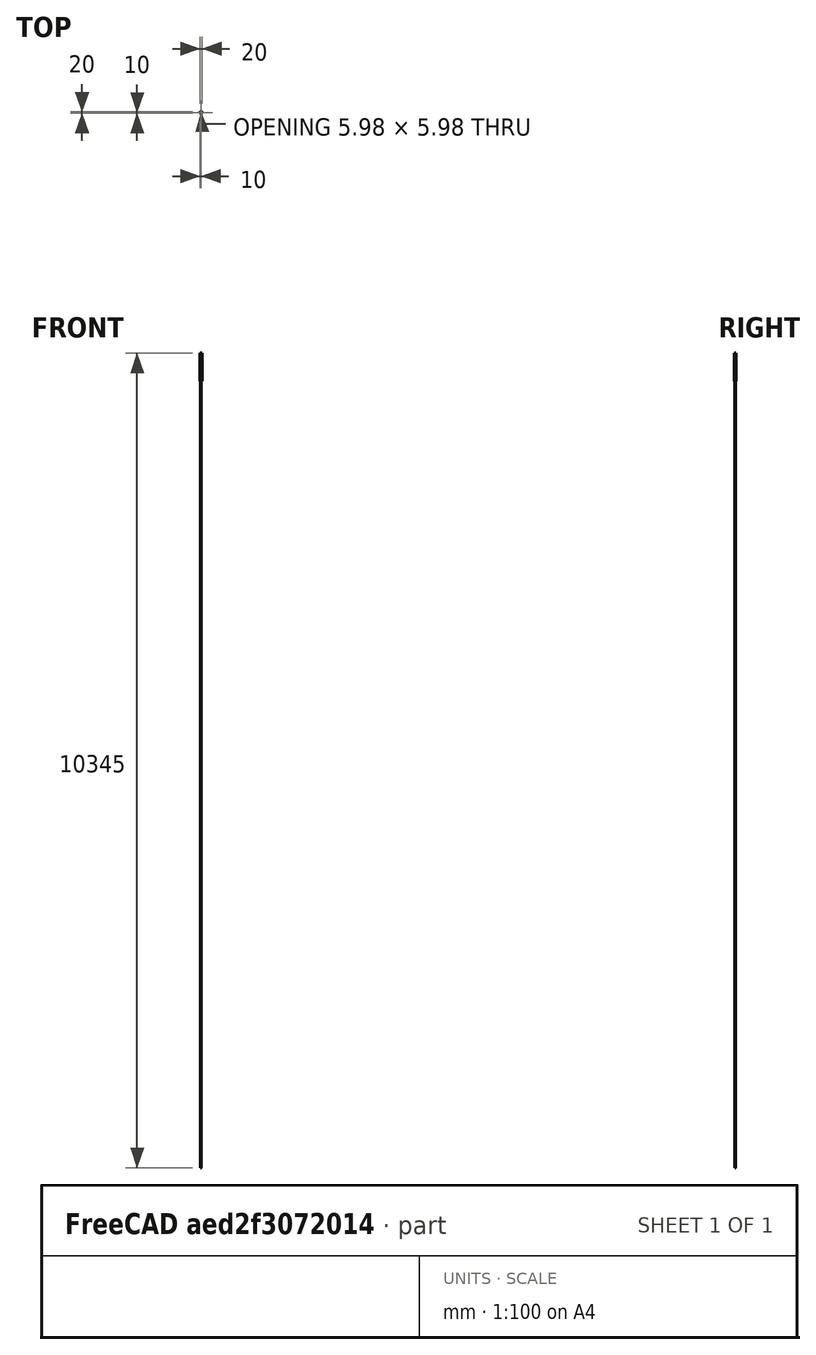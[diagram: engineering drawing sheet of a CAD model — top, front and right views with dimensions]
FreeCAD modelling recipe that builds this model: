
FCSTD DOCUMENT  (FreeCAD 0.15R4671 (Git))
Label: Perfil 350mm
License: CC-BY 3.0
LicenseURL: http://creativecommons.org/licenses/by/3.0/
objects: Sketcher::SketchObject×2, Part::Extrusion×2, PartDesign::Pad×1, PartDesign::Pocket×1, Part::Cut×1
note: 9 computed .brp shape members not serialized (recipe doc carries the construction recipe); baked Part::Feature solids carry a one-line shape summary decoded from their .brp

FEATURE [Sketcher::SketchObject] Sketch
  Placement = pos=(1.5,0,0) rot=(0,0,1;0rad)
  sketch-geometry (136):
    g0: LineSegment StartX=0 StartY=20 StartZ=0 EndX=4.65 EndY=20 EndZ=0
    g1: ArcOfCircle CenterX=-1e-12 CenterY=18.5 CenterZ=0 NormalX=0 NormalY=0 NormalZ=1 Radius=1.5 StartAngle=1.5708 EndAngle=3.14159
    g2: LineSegment StartX=-1.5 StartY=13.85 StartZ=0 EndX=-1.5 EndY=18.5 EndZ=0
    g3: ArcOfCircle CenterX=-1.3 CenterY=13.85 CenterZ=0 NormalX=0 NormalY=0 NormalZ=1 Radius=0.2 StartAngle=3.14159 EndAngle=4.71239
    g4: LineSegment StartX=-1 StartY=13.65 StartZ=0 EndX=-1.3 EndY=13.65 EndZ=0
    g5: LineSegment StartX=-1 StartY=13.3 StartZ=0 EndX=-1 EndY=13.65 EndZ=0
    g6: ArcOfCircle CenterX=-0.8 CenterY=13.3 CenterZ=0 NormalX=0 NormalY=0 NormalZ=1 Radius=0.2 StartAngle=3.14159 EndAngle=4.71239
    g7: LineSegment StartX=-0.5 StartY=13.1 StartZ=0 EndX=-0.8 EndY=13.1 EndZ=0
    g8: ArcOfCircle CenterX=-0.5 CenterY=13.6 CenterZ=0 NormalX=0 NormalY=0 NormalZ=1 Radius=0.5 StartAngle=4.71239 EndAngle=6.28319
    g9: LineSegment StartX=2.68e-07 StartY=15.5 StartZ=0 EndX=2.68e-07 EndY=13.6 EndZ=0
    g10: ArcOfCircle CenterX=0.5 CenterY=15.5 CenterZ=0 NormalX=0 NormalY=0 NormalZ=1 Radius=0.5 StartAngle=1.5708 EndAngle=3.14159
    g11: LineSegment StartX=1.23223 StartY=16 StartZ=0 EndX=0.5 EndY=16 EndZ=0
    g12: ArcOfCircle CenterX=1.23223 CenterY=15.5 CenterZ=0 NormalX=0 NormalY=0 NormalZ=1 Radius=0.5 StartAngle=0.785398 EndAngle=1.5708
    g13: LineSegment StartX=3.85355 StartY=13.5858 StartZ=0 EndX=1.58579 EndY=15.8536 EndZ=0
    g14: ArcOfCircle CenterX=3.5 CenterY=13.2322 CenterZ=0 NormalX=0 NormalY=0 NormalZ=1 Radius=0.5 StartAngle=0 EndAngle=0.785398
    g15: LineSegment StartX=4 StartY=10.9536 StartZ=0 EndX=4 EndY=13.2322 EndZ=0
    g16: ArcOfCircle CenterX=4.2 CenterY=10.9536 CenterZ=0 NormalX=0 NormalY=0 NormalZ=1 Radius=0.2 StartAngle=3.14159 EndAngle=3.66519
    g17: LineSegment StartX=4.46188 StartY=10.1 StartZ=0 EndX=4.0268 EndY=10.8536 EndZ=0
    g18: ArcOfCircle CenterX=4.28868 CenterY=10 CenterZ=0 NormalX=0 NormalY=0 NormalZ=1 Radius=0.2 StartAngle=5.75959 EndAngle=6.80678
    g19: LineSegment StartX=4.0268 StartY=9.14641 StartZ=0 EndX=4.46188 EndY=9.9 EndZ=0
    g20: ArcOfCircle CenterX=4.2 CenterY=9.04641 CenterZ=0 NormalX=0 NormalY=0 NormalZ=1 Radius=0.2 StartAngle=2.61799 EndAngle=3.14159
    g21: LineSegment StartX=4 StartY=6.76777 StartZ=0 EndX=4 EndY=9.04641 EndZ=0
    g22: ArcOfCircle CenterX=3.5 CenterY=6.76777 CenterZ=0 NormalX=0 NormalY=0 NormalZ=1 Radius=0.5 StartAngle=5.49779 EndAngle=6.28319
    g23: LineSegment StartX=1.58579 StartY=4.14645 StartZ=0 EndX=3.85355 EndY=6.41421 EndZ=0
    g24: ArcOfCircle CenterX=1.23223 CenterY=4.5 CenterZ=0 NormalX=0 NormalY=0 NormalZ=1 Radius=0.5 StartAngle=4.71239 EndAngle=5.49779
    g25: LineSegment StartX=0.5 StartY=4 StartZ=0 EndX=1.23223 EndY=4 EndZ=0
    g26: ArcOfCircle CenterX=0.5 CenterY=4.5 CenterZ=0 NormalX=0 NormalY=0 NormalZ=1 Radius=0.5 StartAngle=3.14159 EndAngle=4.71239
    g27: LineSegment StartX=2.68e-07 StartY=6.4 StartZ=0 EndX=2.68e-07 EndY=4.5 EndZ=0
    g28: ArcOfCircle CenterX=-0.5 CenterY=6.4 CenterZ=0 NormalX=0 NormalY=0 NormalZ=1 Radius=0.5 StartAngle=0 EndAngle=1.5708
    g29: LineSegment StartX=-0.8 StartY=6.9 StartZ=0 EndX=-0.5 EndY=6.9 EndZ=0
    g30: ArcOfCircle CenterX=-0.8 CenterY=6.7 CenterZ=0 NormalX=0 NormalY=0 NormalZ=1 Radius=0.2 StartAngle=1.5708 EndAngle=3.14159
    g31: LineSegment StartX=-1 StartY=6.35 StartZ=0 EndX=-1 EndY=6.7 EndZ=0
    g32: LineSegment StartX=-1.3 StartY=6.35 StartZ=0 EndX=-1 EndY=6.35 EndZ=0
    g33: ArcOfCircle CenterX=-1.3 CenterY=6.15 CenterZ=0 NormalX=0 NormalY=0 NormalZ=1 Radius=0.2 StartAngle=1.5708 EndAngle=3.14159
    g34: LineSegment StartX=-1.5 StartY=1.5 StartZ=0 EndX=-1.5 EndY=6.15 EndZ=0
    g35: ArcOfCircle CenterX=0 CenterY=1.5 CenterZ=0 NormalX=0 NormalY=0 NormalZ=1 Radius=1.5 StartAngle=3.14159 EndAngle=4.71239
    g36: LineSegment StartX=4.65 StartY=1e-12 StartZ=0 EndX=0 EndY=0 EndZ=0
    g37: ArcOfCircle CenterX=4.65 CenterY=0.2 CenterZ=0 NormalX=0 NormalY=0 NormalZ=1 Radius=0.2 StartAngle=4.71239 EndAngle=6.28319
    g38: LineSegment StartX=4.85 StartY=0.5 StartZ=0 EndX=4.85 EndY=0.2 EndZ=0
    g39: LineSegment StartX=5.2 StartY=0.5 StartZ=0 EndX=4.85 EndY=0.5 EndZ=0
    g40: ArcOfCircle CenterX=5.2 CenterY=0.7 CenterZ=0 NormalX=0 NormalY=0 NormalZ=1 Radius=0.2 StartAngle=4.71239 EndAngle=6.28319
    g41: LineSegment StartX=5.4 StartY=1 StartZ=0 EndX=5.4 EndY=0.7 EndZ=0
    g42: ArcOfCircle CenterX=4.9 CenterY=1 CenterZ=0 NormalX=0 NormalY=0 NormalZ=1 Radius=0.5 StartAngle=0 EndAngle=1.5708
    g43: LineSegment StartX=3 StartY=1.5 StartZ=0 EndX=4.9 EndY=1.5 EndZ=0
    g44: ArcOfCircle CenterX=3 CenterY=2 CenterZ=0 NormalX=0 NormalY=0 NormalZ=1 Radius=0.5 StartAngle=3.14159 EndAngle=4.71239
    g45: LineSegment StartX=2.5 StartY=2.73223 StartZ=0 EndX=2.5 EndY=2 EndZ=0
    g46: ArcOfCircle CenterX=3 CenterY=2.73223 CenterZ=0 NormalX=0 NormalY=0 NormalZ=1 Radius=0.5 StartAngle=2.35619 EndAngle=3.14159
    g47: LineSegment StartX=4.91421 StartY=5.35355 StartZ=0 EndX=2.64645 EndY=3.08579 EndZ=0
    g48: ArcOfCircle CenterX=5.26777 CenterY=5 CenterZ=0 NormalX=0 NormalY=0 NormalZ=1 Radius=0.5 StartAngle=1.5708 EndAngle=2.35619
    g49: LineSegment StartX=7.54641 StartY=5.5 StartZ=0 EndX=5.26777 EndY=5.5 EndZ=0
    g50: ArcOfCircle CenterX=7.54641 CenterY=5.7 CenterZ=0 NormalX=0 NormalY=0 NormalZ=1 Radius=0.2 StartAngle=4.71239 EndAngle=5.23599
    g51: LineSegment StartX=8.4 StartY=5.96188 StartZ=0 EndX=7.64641 EndY=5.52679 EndZ=0
    g52: ArcOfCircle CenterX=8.5 CenterY=5.78868 CenterZ=0 NormalX=0 NormalY=0 NormalZ=1 Radius=0.2 StartAngle=1.0472 EndAngle=2.0944
    g53: LineSegment StartX=9.35359 StartY=5.52679 StartZ=0 EndX=8.6 EndY=5.96188 EndZ=0
    g54: ArcOfCircle CenterX=9.45359 CenterY=5.7 CenterZ=0 NormalX=0 NormalY=0 NormalZ=1 Radius=0.2 StartAngle=4.18879 EndAngle=4.71239
    g55: LineSegment StartX=11.7322 StartY=5.5 StartZ=0 EndX=9.45359 EndY=5.5 EndZ=0
    g56: ArcOfCircle CenterX=11.7322 CenterY=5 CenterZ=0 NormalX=0 NormalY=0 NormalZ=1 Radius=0.5 StartAngle=0.785398 EndAngle=1.5708
    g57: LineSegment StartX=14.3536 StartY=3.08579 StartZ=0 EndX=12.0858 EndY=5.35355 EndZ=0
    g58: ArcOfCircle CenterX=14 CenterY=2.73223 CenterZ=0 NormalX=0 NormalY=0 NormalZ=1 Radius=0.5 StartAngle=0 EndAngle=0.785398
    g59: LineSegment StartX=14.5 StartY=2 StartZ=0 EndX=14.5 EndY=2.73223 EndZ=0
    g60: ArcOfCircle CenterX=14 CenterY=2 CenterZ=0 NormalX=0 NormalY=0 NormalZ=1 Radius=0.5 StartAngle=4.71239 EndAngle=6.28319
    g61: LineSegment StartX=12.1 StartY=1.5 StartZ=0 EndX=14 EndY=1.5 EndZ=0
    g62: ArcOfCircle CenterX=12.1 CenterY=1 CenterZ=0 NormalX=0 NormalY=0 NormalZ=1 Radius=0.5 StartAngle=1.5708 EndAngle=3.14159
    g63: LineSegment StartX=11.6 StartY=0.7 StartZ=0 EndX=11.6 EndY=1 EndZ=0
    g64: ArcOfCircle CenterX=11.8 CenterY=0.7 CenterZ=0 NormalX=0 NormalY=0 NormalZ=1 Radius=0.2 StartAngle=3.14159 EndAngle=4.71239
    g65: LineSegment StartX=12.15 StartY=0.5 StartZ=0 EndX=11.8 EndY=0.5 EndZ=0
    g66: LineSegment StartX=12.15 StartY=0.2 StartZ=0 EndX=12.15 EndY=0.5 EndZ=0
    g67: ArcOfCircle CenterX=12.35 CenterY=0.2 CenterZ=0 NormalX=0 NormalY=0 NormalZ=1 Radius=0.2 StartAngle=3.14159 EndAngle=4.71239
    g68: LineSegment StartX=17 StartY=1e-12 StartZ=0 EndX=12.35 EndY=0 EndZ=0
    g69: ArcOfCircle CenterX=17 CenterY=1.5 CenterZ=0 NormalX=0 NormalY=0 NormalZ=1 Radius=1.5 StartAngle=4.71239 EndAngle=6.28319
    g70: LineSegment StartX=18.5 StartY=6.15 StartZ=0 EndX=18.5 EndY=1.5 EndZ=0
    g71: ArcOfCircle CenterX=18.3 CenterY=6.15 CenterZ=0 NormalX=0 NormalY=0 NormalZ=1 Radius=0.2 StartAngle=0 EndAngle=1.5708
    g72: LineSegment StartX=18 StartY=6.35 StartZ=0 EndX=18.3 EndY=6.35 EndZ=0
    g73: LineSegment StartX=18 StartY=6.7 StartZ=0 EndX=18 EndY=6.35 EndZ=0
    g74: ArcOfCircle CenterX=17.8 CenterY=6.7 CenterZ=0 NormalX=0 NormalY=0 NormalZ=1 Radius=0.2 StartAngle=0 EndAngle=1.5708
    g75: LineSegment StartX=17.5 StartY=6.9 StartZ=0 EndX=17.8 EndY=6.9 EndZ=0
    g76: ArcOfCircle CenterX=17.5 CenterY=6.4 CenterZ=0 NormalX=0 NormalY=0 NormalZ=1 Radius=0.5 StartAngle=1.5708 EndAngle=3.14159
    g77: LineSegment StartX=17 StartY=4.5 StartZ=0 EndX=17 EndY=6.4 EndZ=0
    g78: ArcOfCircle CenterX=16.5 CenterY=4.5 CenterZ=0 NormalX=0 NormalY=0 NormalZ=1 Radius=0.5 StartAngle=4.71239 EndAngle=6.28319
    g79: LineSegment StartX=15.7678 StartY=4 StartZ=0 EndX=16.5 EndY=4 EndZ=0
    g80: ArcOfCircle CenterX=15.7678 CenterY=4.5 CenterZ=0 NormalX=0 NormalY=0 NormalZ=1 Radius=0.5 StartAngle=3.92699 EndAngle=4.71239
    g81: LineSegment StartX=13.1464 StartY=6.41421 StartZ=0 EndX=15.4142 EndY=4.14645 EndZ=0
    g82: ArcOfCircle CenterX=13.5 CenterY=6.76777 CenterZ=0 NormalX=0 NormalY=0 NormalZ=1 Radius=0.5 StartAngle=3.14159 EndAngle=3.92699
    g83: LineSegment StartX=13 StartY=9.04641 StartZ=0 EndX=13 EndY=6.76777 EndZ=0
    g84: ArcOfCircle CenterX=12.8 CenterY=9.04641 CenterZ=0 NormalX=0 NormalY=0 NormalZ=1 Radius=0.2 StartAngle=0 EndAngle=0.523599
    g85: LineSegment StartX=12.5381 StartY=9.9 StartZ=0 EndX=12.9732 EndY=9.14641 EndZ=0
    g86: ArcOfCircle CenterX=12.7113 CenterY=10 CenterZ=0 NormalX=0 NormalY=0 NormalZ=1 Radius=0.2 StartAngle=2.61799 EndAngle=3.66519
    g87: LineSegment StartX=12.9732 StartY=10.8536 StartZ=0 EndX=12.5381 EndY=10.1 EndZ=0
    g88: ArcOfCircle CenterX=12.8 CenterY=10.9536 CenterZ=0 NormalX=0 NormalY=0 NormalZ=1 Radius=0.2 StartAngle=5.75959 EndAngle=6.28319
    g89: LineSegment StartX=13 StartY=13.2322 StartZ=0 EndX=13 EndY=10.9536 EndZ=0
    g90: ArcOfCircle CenterX=13.5 CenterY=13.2322 CenterZ=0 NormalX=0 NormalY=0 NormalZ=1 Radius=0.5 StartAngle=2.35619 EndAngle=3.14159
    g91: LineSegment StartX=15.4142 StartY=15.8536 StartZ=0 EndX=13.1464 EndY=13.5858 EndZ=0
    g92: ArcOfCircle CenterX=15.7678 CenterY=15.5 CenterZ=0 NormalX=0 NormalY=0 NormalZ=1 Radius=0.5 StartAngle=1.5708 EndAngle=2.35619
    g93: LineSegment StartX=16.5 StartY=16 StartZ=0 EndX=15.7678 EndY=16 EndZ=0
    g94: ArcOfCircle CenterX=16.5 CenterY=15.5 CenterZ=0 NormalX=0 NormalY=0 NormalZ=1 Radius=0.5 StartAngle=0 EndAngle=1.5708
    g95: LineSegment StartX=17 StartY=13.6 StartZ=0 EndX=17 EndY=15.5 EndZ=0
    g96: ArcOfCircle CenterX=17.5 CenterY=13.6 CenterZ=0 NormalX=0 NormalY=0 NormalZ=1 Radius=0.5 StartAngle=3.14159 EndAngle=4.71239
    g97: LineSegment StartX=17.8 StartY=13.1 StartZ=0 EndX=17.5 EndY=13.1 EndZ=0
    g98: ArcOfCircle CenterX=17.8 CenterY=13.3 CenterZ=0 NormalX=0 NormalY=0 NormalZ=1 Radius=0.2 StartAngle=4.71239 EndAngle=6.28319
    g99: LineSegment StartX=18 StartY=13.65 StartZ=0 EndX=18 EndY=13.3 EndZ=0
    g100: LineSegment StartX=18.3 StartY=13.65 StartZ=0 EndX=18 EndY=13.65 EndZ=0
    g101: ArcOfCircle CenterX=18.3 CenterY=13.85 CenterZ=0 NormalX=0 NormalY=0 NormalZ=1 Radius=0.2 StartAngle=4.71239 EndAngle=6.28319
    g102: LineSegment StartX=18.5 StartY=18.5 StartZ=0 EndX=18.5 EndY=13.85 EndZ=0
    g103: ArcOfCircle CenterX=17 CenterY=18.5 CenterZ=0 NormalX=0 NormalY=0 NormalZ=1 Radius=1.5 StartAngle=0 EndAngle=1.5708
    g104: LineSegment StartX=12.35 StartY=20 StartZ=0 EndX=17 EndY=20 EndZ=0
    g105: ArcOfCircle CenterX=12.35 CenterY=19.8 CenterZ=0 NormalX=0 NormalY=0 NormalZ=1 Radius=0.2 StartAngle=1.5708 EndAngle=3.14159
    g106: LineSegment StartX=12.15 StartY=19.5 StartZ=0 EndX=12.15 EndY=19.8 EndZ=0
    g107: LineSegment StartX=11.8 StartY=19.5 StartZ=0 EndX=12.15 EndY=19.5 EndZ=0
    g108: ArcOfCircle CenterX=11.8 CenterY=19.3 CenterZ=0 NormalX=0 NormalY=0 NormalZ=1 Radius=0.2 StartAngle=1.5708 EndAngle=3.14159
    g109: LineSegment StartX=11.6 StartY=19 StartZ=0 EndX=11.6 EndY=19.3 EndZ=0
    g110: ArcOfCircle CenterX=12.1 CenterY=19 CenterZ=0 NormalX=0 NormalY=0 NormalZ=1 Radius=0.5 StartAngle=3.14159 EndAngle=4.71239
    g111: LineSegment StartX=14 StartY=18.5 StartZ=0 EndX=12.1 EndY=18.5 EndZ=0
    g112: ArcOfCircle CenterX=14 CenterY=18 CenterZ=0 NormalX=0 NormalY=0 NormalZ=1 Radius=0.5 StartAngle=0 EndAngle=1.5708
    g113: LineSegment StartX=14.5 StartY=17.2678 StartZ=0 EndX=14.5 EndY=18 EndZ=0
    g114: ArcOfCircle CenterX=14 CenterY=17.2678 CenterZ=0 NormalX=0 NormalY=0 NormalZ=1 Radius=0.5 StartAngle=5.49779 EndAngle=6.28319
    g115: LineSegment StartX=12.0858 StartY=14.6464 StartZ=0 EndX=14.3536 EndY=16.9142 EndZ=0
    g116: ArcOfCircle CenterX=11.7322 CenterY=15 CenterZ=0 NormalX=0 NormalY=0 NormalZ=1 Radius=0.5 StartAngle=4.71239 EndAngle=5.49779
    g117: LineSegment StartX=9.45359 StartY=14.5 StartZ=0 EndX=11.7322 EndY=14.5 EndZ=0
    g118: ArcOfCircle CenterX=9.45359 CenterY=14.3 CenterZ=0 NormalX=0 NormalY=0 NormalZ=1 Radius=0.2 StartAngle=1.5708 EndAngle=2.0944
    g119: LineSegment StartX=8.6 StartY=14.0381 StartZ=0 EndX=9.35359 EndY=14.4732 EndZ=0
    g120: ArcOfCircle CenterX=8.5 CenterY=14.2113 CenterZ=0 NormalX=0 NormalY=0 NormalZ=1 Radius=0.2 StartAngle=4.18879 EndAngle=5.23599
    g121: LineSegment StartX=7.64641 StartY=14.4732 StartZ=0 EndX=8.4 EndY=14.0381 EndZ=0
    g122: ArcOfCircle CenterX=7.54641 CenterY=14.3 CenterZ=0 NormalX=0 NormalY=0 NormalZ=1 Radius=0.2 StartAngle=1.0472 EndAngle=1.5708
    g123: LineSegment StartX=5.26777 StartY=14.5 StartZ=0 EndX=7.54641 EndY=14.5 EndZ=0
    g124: ArcOfCircle CenterX=5.26777 CenterY=15 CenterZ=0 NormalX=0 NormalY=0 NormalZ=1 Radius=0.5 StartAngle=3.92699 EndAngle=4.71239
    g125: LineSegment StartX=2.64645 StartY=16.9142 StartZ=0 EndX=4.91421 EndY=14.6464 EndZ=0
    g126: ArcOfCircle CenterX=3 CenterY=17.2678 CenterZ=0 NormalX=0 NormalY=0 NormalZ=1 Radius=0.5 StartAngle=3.14159 EndAngle=3.92699
    g127: LineSegment StartX=2.5 StartY=18 StartZ=0 EndX=2.5 EndY=17.2678 EndZ=0
    g128: ArcOfCircle CenterX=3 CenterY=18 CenterZ=0 NormalX=0 NormalY=0 NormalZ=1 Radius=0.5 StartAngle=1.5708 EndAngle=3.14159
    g129: LineSegment StartX=4.9 StartY=18.5 StartZ=0 EndX=3 EndY=18.5 EndZ=0
    g130: ArcOfCircle CenterX=4.9 CenterY=19 CenterZ=0 NormalX=0 NormalY=0 NormalZ=1 Radius=0.5 StartAngle=4.71239 EndAngle=6.28319
    g131: LineSegment StartX=5.4 StartY=19.3 StartZ=0 EndX=5.4 EndY=19 EndZ=0
    g132: ArcOfCircle CenterX=5.2 CenterY=19.3 CenterZ=0 NormalX=0 NormalY=0 NormalZ=1 Radius=0.2 StartAngle=0 EndAngle=1.5708
    g133: LineSegment StartX=4.85 StartY=19.5 StartZ=0 EndX=5.2 EndY=19.5 EndZ=0
    g134: LineSegment StartX=4.85 StartY=19.8 StartZ=0 EndX=4.85 EndY=19.5 EndZ=0
    g135: ArcOfCircle CenterX=4.65 CenterY=19.8 CenterZ=0 NormalX=0 NormalY=0 NormalZ=1 Radius=0.2 StartAngle=0 EndAngle=1.5708
  constraints (136):
    c: Coincident(g0,g1)
    c: Coincident(g135,g0)
    c: Coincident(g1,g2)
    c: Coincident(g2,g3)
    c: Coincident(g3,g4)
    c: Coincident(g4,g5)
    c: Coincident(g6,g5)
    c: Coincident(g7,g6)
    c: Coincident(g8,g7)
    c: Coincident(g9,g8)
    c: Coincident(g10,g9)
    c: Coincident(g10,g11)
    c: Coincident(g11,g12)
    c: Coincident(g12,g13)
    c: Coincident(g14,g13)
    c: Coincident(g15,g14)
    c: Coincident(g15,g16)
    c: Coincident(g16,g17)
    c: Coincident(g17,g18)
    c: Coincident(g18,g19)
    c: Coincident(g19,g20)
    c: Coincident(g20,g21)
    c: Coincident(g21,g22)
    c: Coincident(g22,g23)
    c: Coincident(g23,g24)
    c: Coincident(g24,g25)
    c: Coincident(g26,g25)
    c: Coincident(g26,g27)
    c: Coincident(g28,g27)
    c: Coincident(g28,g29)
    c: Coincident(g30,g29)
    c: Coincident(g31,g30)
    c: Coincident(g31,g32)
    c: Coincident(g32,g33)
    c: Coincident(g33,g34)
    c: Coincident(g35,g34)
    c: Coincident(g36,g35)
    c: Coincident(g37,g36)
    c: Coincident(g37,g38)
    c: Coincident(g38,g39)
    c: Coincident(g40,g39)
    c: Coincident(g40,g41)
    c: Coincident(g41,g42)
    c: Coincident(g43,g42)
    c: Coincident(g44,g43)
    c: Coincident(g44,g45)
    c: Coincident(g45,g46)
    c: Coincident(g46,g47)
    c: Coincident(g47,g48)
    c: Coincident(g49,g48)
    c: Coincident(g49,g50)
    c: Coincident(g50,g51)
    c: Coincident(g51,g52)
    c: Coincident(g53,g52)
    c: Coincident(g54,g53)
    c: Coincident(g55,g54)
    c: Coincident(g56,g55)
    c: Coincident(g56,g57)
    c: Coincident(g58,g57)
    c: Coincident(g59,g58)
    c: Coincident(g60,g59)
    c: Coincident(g61,g60)
    c: Coincident(g62,g61)
    c: Coincident(g62,g63)
    c: Coincident(g64,g63)
    c: Coincident(g65,g64)
    c: Coincident(g66,g65)
    c: Coincident(g67,g66)
    c: Coincident(g67,g68)
    c: Coincident(g69,g68)
    c: Coincident(g70,g69)
    c: Coincident(g71,g70)
    c: Coincident(g72,g71)
    c: Coincident(g73,g72)
    c: Coincident(g73,g74)
    c: Coincident(g75,g74)
    c: Coincident(g76,g75)
    c: Coincident(g76,g77)
    c: Coincident(g77,g78)
    c: Coincident(g78,g79)
    c: Coincident(g80,g79)
    c: Coincident(g81,g80)
    c: Coincident(g81,g82)
    c: Coincident(g82,g83)
    c: Coincident(g83,g84)
    c: Coincident(g85,g84)
    c: Coincident(g86,g85)
    c: Coincident(g86,g87)
    c: Coincident(g88,g87)
    c: Coincident(g88,g89)
    c: Coincident(g89,g90)
    c: Coincident(g91,g90)
    c: Coincident(g92,g91)
    c: Coincident(g93,g92)
    c: Coincident(g94,g93)
    c: Coincident(g94,g95)
    c: Coincident(g95,g96)
    c: Coincident(g96,g97)
    c: Coincident(g98,g97)
    c: Coincident(g98,g99)
    c: Coincident(g100,g99)
    c: Coincident(g100,g101)
    c: Coincident(g101,g102)
    c: Coincident(g102,g103)
    c: Coincident(g103,g104)
    c: Coincident(g104,g105)
    c: Coincident(g106,g105)
    c: Coincident(g107,g106)
    c: Coincident(g108,g107)
    c: Coincident(g109,g108)
    c: Coincident(g110,g109)
    c: Coincident(g111,g110)
    c: Coincident(g112,g111)
    c: Coincident(g112,g113)
    c: Coincident(g113,g114)
    c: Coincident(g114,g115)
    c: Coincident(g115,g116)
    c: Coincident(g117,g116)
    c: Coincident(g118,g117)
    c: Coincident(g119,g118)
    c: Coincident(g119,g120)
    c: Coincident(g121,g120)
    c: Coincident(g121,g122)
    c: Coincident(g122,g123)
    c: Coincident(g124,g123)
    c: Coincident(g124,g125)
    c: Coincident(g126,g125)
    c: Coincident(g127,g126)
    c: Coincident(g128,g127)
    c: Coincident(g129,g128)
    c: Coincident(g130,g129)
    c: Coincident(g130,g131)
    c: Coincident(g131,g132)
    c: Coincident(g133,g132)
    c: Coincident(g134,g133)
    c: Coincident(g135,g134)
FEATURE [PartDesign::Pad] Pad
  Length = 5
  Length2 = 100
  Placement = pos=(1.5,0,0) rot=(0,0,1;0rad)
  Sketch = -> Sketch
  Type = 0
FEATURE [Sketcher::SketchObject] Sketch001
  Placement = pos=(1.5,0,5) rot=(0,0,1;0rad)
  Support = -> Pad [Face138]
  sketch-geometry (16):
    g0: ArcOfCircle CenterX=8.5 CenterY=10 CenterZ=0 NormalX=0 NormalY=0 NormalZ=1 Radius=3.54978 StartAngle=2.14023 EndAngle=2.57348
    g1: LineSegment StartX=6.5861 StartY=12.9896 StartZ=0 EndX=7.24181 EndY=12.4453 EndZ=0
    g2: ArcOfCircle CenterX=8.5 CenterY=10 CenterZ=0 NormalX=0 NormalY=0 NormalZ=1 Radius=2.75 StartAngle=1.09559 EndAngle=2.046
    g3: LineSegment StartX=9.75819 StartY=12.4453 StartZ=0 EndX=10.4139 EndY=12.9896 EndZ=0
    g4: ArcOfCircle CenterX=8.5 CenterY=10 CenterZ=0 NormalX=0 NormalY=0 NormalZ=1 Radius=3.54978 StartAngle=0.568112 EndAngle=1.00136
    g5: LineSegment StartX=11.4922 StartY=11.9099 StartZ=0 EndX=10.9453 EndY=11.2582 EndZ=0
    g6: ArcOfCircle CenterX=8.5 CenterY=10 CenterZ=0 NormalX=0 NormalY=0 NormalZ=1 Radius=2.75 StartAngle=5.80798 EndAngle=6.75839
    g7: LineSegment StartX=10.9453 StartY=8.74181 StartZ=0 EndX=11.4922 EndY=8.09007 EndZ=0
    g8: ArcOfCircle CenterX=8.5 CenterY=10 CenterZ=0 NormalX=0 NormalY=0 NormalZ=1 Radius=3.54978 StartAngle=5.28183 EndAngle=5.71507
    g9: LineSegment StartX=10.4139 StartY=7.01036 StartZ=0 EndX=9.75819 EndY=7.5547 EndZ=0
    g10: ArcOfCircle CenterX=8.5 CenterY=10 CenterZ=0 NormalX=0 NormalY=0 NormalZ=1 Radius=2.75 StartAngle=4.23718 EndAngle=5.1876
    g11: LineSegment StartX=7.24181 StartY=7.5547 StartZ=0 EndX=6.5861 EndY=7.01036 EndZ=0
    g12: ArcOfCircle CenterX=8.5 CenterY=10 CenterZ=0 NormalX=0 NormalY=0 NormalZ=1 Radius=3.54978 StartAngle=3.7097 EndAngle=4.14295
    g13: LineSegment StartX=5.50783 StartY=8.09007 StartZ=0 EndX=6.0547 EndY=8.74181 EndZ=0
    g14: ArcOfCircle CenterX=8.5 CenterY=10 CenterZ=0 NormalX=0 NormalY=0 NormalZ=1 Radius=2.75 StartAngle=2.66639 EndAngle=3.6168
    g15: LineSegment StartX=6.0547 StartY=11.2582 StartZ=0 EndX=5.50783 EndY=11.9099 EndZ=0
  constraints (16):
    c: Coincident(g0,g1)
    c: Coincident(g15,g0)
    c: Coincident(g1,g2)
    c: Coincident(g3,g2)
    c: Coincident(g4,g3)
    c: Coincident(g4,g5)
    c: Coincident(g6,g5)
    c: Coincident(g7,g6)
    c: Coincident(g8,g7)
    c: Coincident(g9,g8)
    c: Coincident(g10,g9)
    c: Coincident(g11,g10)
    c: Coincident(g12,g11)
    c: Coincident(g13,g12)
    c: Coincident(g14,g13)
    c: Coincident(g15,g14)
FEATURE [PartDesign::Pocket] Pocket
  Length = 5
  Placement = pos=(1.5,0,0) rot=(0,0,1;0rad)
  Sketch = -> Sketch001
  Type = 1
FEATURE [Part::Extrusion] Extrude001
  Base = -> Sketch001
  Dir = (0,0,470)
  Placement = pos=(0,0,-25) rot=(0,0,1;0rad)
  Solid = true
FEATURE [Part::Extrusion] Extrude002
  Base = -> Sketch
  Dir = (0,0,350)
  Solid = true
FEATURE [Part::Cut] Cut
  Base = -> Extrude002
  Tool = -> Extrude001
